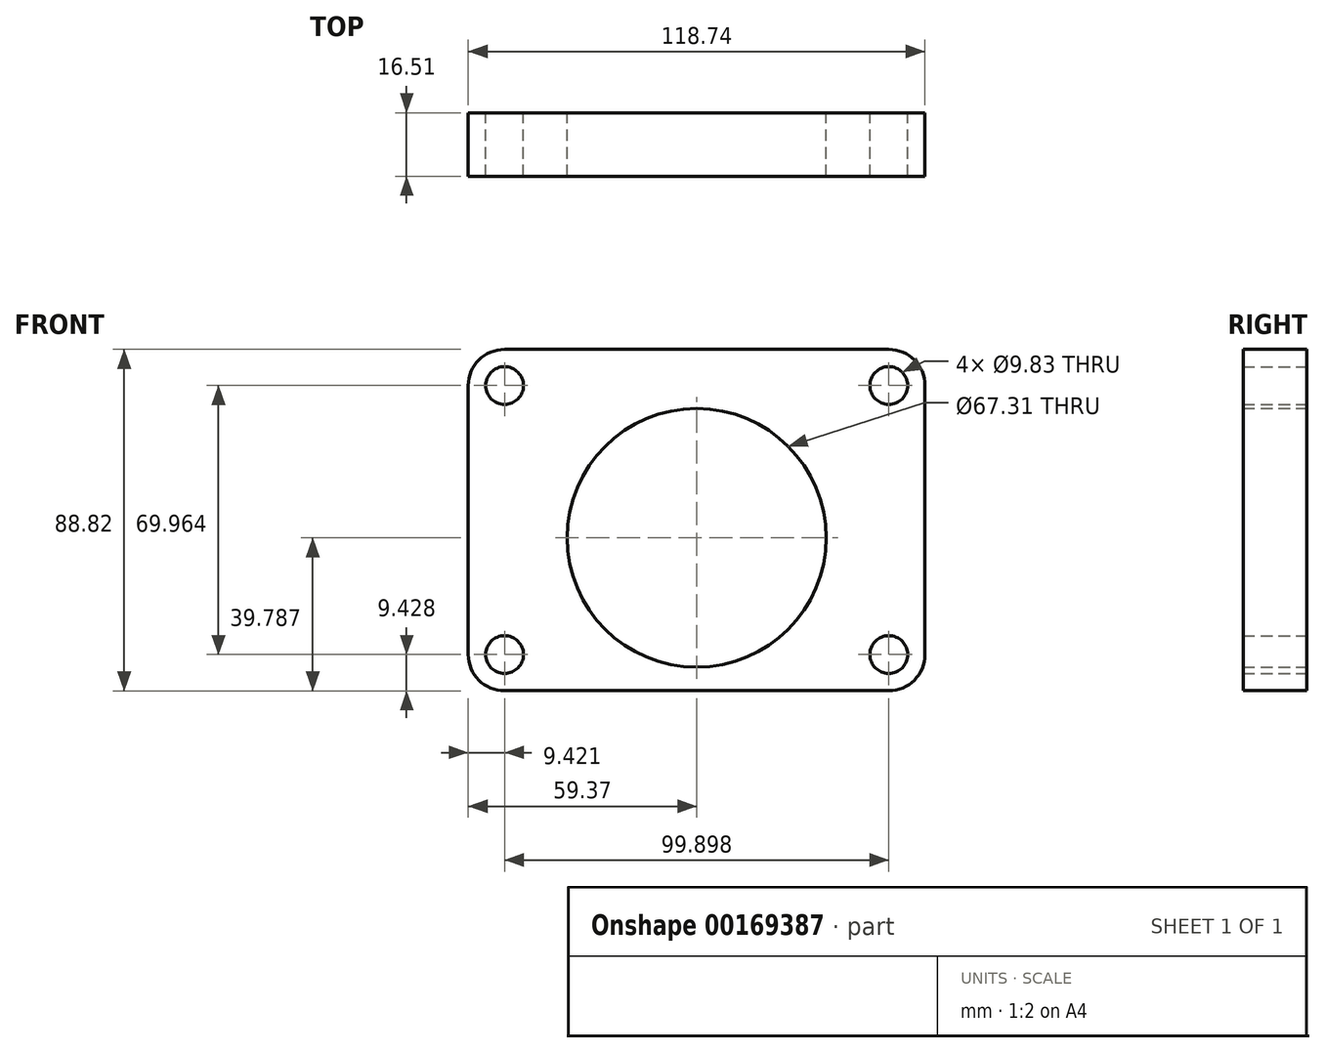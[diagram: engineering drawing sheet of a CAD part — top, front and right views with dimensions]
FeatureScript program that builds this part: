
annotation { "Feature Type Name" : "Feature", "Feature Type Description" : "" }
export const myFeature = defineFeature(function(context is Context, id is Id, definition is map)
    precondition{}
    {
        {
            var Q0;
            Q0=qCreatedBy(makeId("Front.planeOp"),FACE);
            var sketch = newSketch(context, id + "F0", { "sketchPlane" : qUnion([Q0])});
            skLineSegment(sketch, "E0.bottom", {"start": v(-49.95, 44.4) * mm, "end": v(49.95, 44.4) * mm});
            skLineSegment(sketch, "E0.top", {"start": v(-49.95, -44.4) * mm, "end": v(49.95, -44.4) * mm});
            skLineSegment(sketch, "E0.left", {"start": v(-59.37, 34.98) * mm, "end": v(-59.37, -34.98) * mm});
            skLineSegment(sketch, "E0.right", {"start": v(59.37, 34.98) * mm, "end": v(59.37, -34.98) * mm});
            skPoint(sketch, "E0.middle", {"position": v(0, 0) * mm});
            skLineSegment(sketch, "E1.bottom", {"start": v(-49.95, 34.98) * mm, "end": v(49.95, 34.98) * mm, "construction": true});
            skLineSegment(sketch, "E1.top", {"start": v(-49.95, -34.98) * mm, "end": v(49.95, -34.98) * mm, "construction": true});
            skLineSegment(sketch, "E1.left", {"start": v(-49.95, 34.98) * mm, "end": v(-49.95, -34.98) * mm, "construction": true});
            skLineSegment(sketch, "E1.right", {"start": v(49.95, 34.98) * mm, "end": v(49.95, -34.98) * mm, "construction": true});
            skCircle(sketch, "E2", {"center": v(-49.95, 34.98) * mm, "radius": 4.91 * mm});
            skCircle(sketch, "E3", {"center": v(49.95, 34.98) * mm, "radius": 4.91 * mm});
            skCircle(sketch, "E4", {"center": v(49.95, -34.98) * mm, "radius": 4.91 * mm});
            skCircle(sketch, "E5", {"center": v(-49.95, -34.98) * mm, "radius": 4.91 * mm});
            skCircle(sketch, "E6", {"center": v(-49.95, 34.98) * mm, "radius": 4.03 * mm, "construction": true});
            skCircle(sketch, "E7", {"center": v(-49.95, -34.98) * mm, "radius": 4.03 * mm, "construction": true});
            skCircle(sketch, "E8", {"center": v(49.95, -34.98) * mm, "radius": 4.03 * mm, "construction": true});
            skCircle(sketch, "E9", {"center": v(49.95, 34.98) * mm, "radius": 4.03 * mm, "construction": true});
            skPoint(sketch, "E10.visualSharp", {"position": v(-59.37, 44.4) * mm});
            skArc(sketch, "E10.filletArc", {"start": v(-49.95, 44.4) * mm, "mid": v(-56.61, 41.65) * mm, "end": v(-59.37, 34.98) * mm});
            skPoint(sketch, "E11.visualSharp", {"position": v(59.37, 44.4) * mm});
            skArc(sketch, "E11.filletArc", {"start": v(59.37, 34.98) * mm, "mid": v(56.61, 41.65) * mm, "end": v(49.95, 44.4) * mm});
            skPoint(sketch, "E12.visualSharp", {"position": v(59.37, -44.4) * mm});
            skArc(sketch, "E12.filletArc", {"start": v(49.95, -44.4) * mm, "mid": v(56.61, -41.65) * mm, "end": v(59.37, -34.98) * mm});
            skPoint(sketch, "E13.visualSharp", {"position": v(-59.37, -44.4) * mm});
            skArc(sketch, "E13.filletArc", {"start": v(-59.37, -34.98) * mm, "mid": v(-56.61, -41.65) * mm, "end": v(-49.95, -44.4) * mm});
            skCircle(sketch, "E14", {"center": v(0, -4.62) * mm, "radius": 28.58 * mm, "construction": true});
            skCircle(sketch, "E15", {"center": v(0, -4.62) * mm, "radius": 33.66 * mm});
            skSolve(sketch);
        }
        {
            var Q0;
            Q0=qSketchRegion(id+"F0",true);
            extrude(context, id + "F1", {"entities" : qUnion([Q0]), "depth" : 16.5 * mm});
        }
    });
